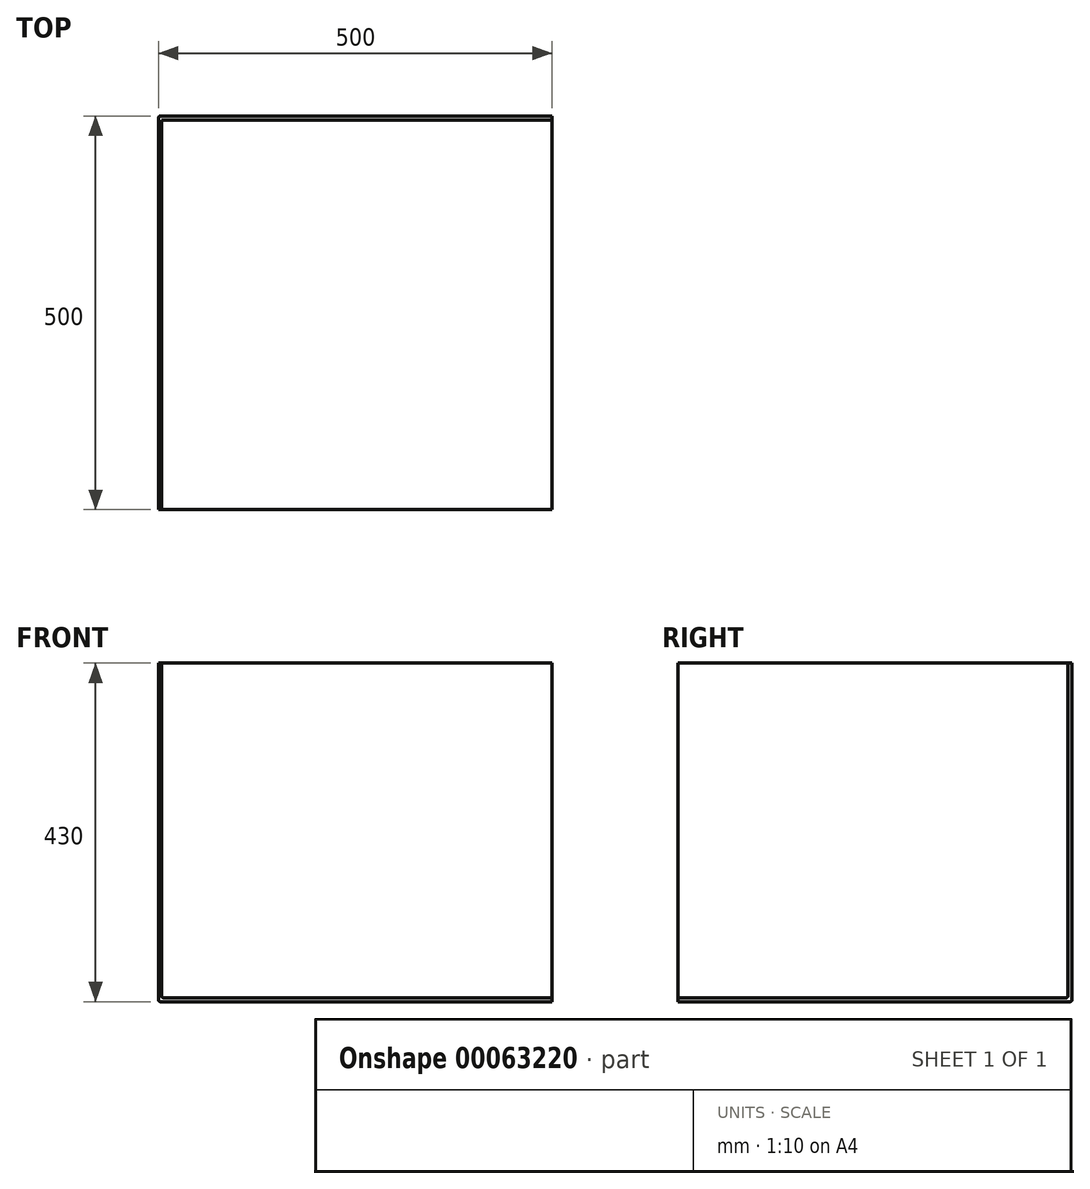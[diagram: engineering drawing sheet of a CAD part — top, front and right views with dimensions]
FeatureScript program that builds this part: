
annotation { "Feature Type Name" : "Feature", "Feature Type Description" : "" }
export const myFeature = defineFeature(function(context is Context, id is Id, definition is map)
    precondition{}
    {
        {
            var Q0;
            Q0=qCreatedBy(makeId("Right.planeOp"),FACE);
            var sketch = newSketch(context, id + "F0", { "sketchPlane" : qUnion([Q0])});
            skLineSegment(sketch, "E0.bottom", {"start": v(0, 0) * mm, "end": v(-5, 0) * mm});
            skLineSegment(sketch, "E0.top", {"start": v(0, 430) * mm, "end": v(-5, 430) * mm});
            skLineSegment(sketch, "E0.left", {"start": v(0, 0) * mm, "end": v(0, 430) * mm});
            skLineSegment(sketch, "E0.right", {"start": v(-5, 0) * mm, "end": v(-5, 430) * mm});
            skSolve(sketch);
        }
        {
            var Q0;
            Q0=makeQuery(id+"F0.imprint","IMPRINT",FACE,{"disambiguationData":[TD([[makeQuery(id+"F0.imprint","IMPRINT",EDGE,{"derivedFrom":sQuery(id+"F0.wireOp",EDGE,"E0.bottom")}),-1.0]])]});
            extrude(context, id + "F1", {"entities" : qUnion([Q0]), "depth" : 500 * mm});
        }
        {
            var Q0;
            Q0=qCreatedBy(makeId("Top.planeOp"),FACE);
            var sketch = newSketch(context, id + "F2", { "sketchPlane" : qUnion([Q0])});
            skLineSegment(sketch, "E1.bottom", {"start": v(0, 0) * mm, "end": v(500, 0) * mm});
            skLineSegment(sketch, "E1.top", {"start": v(0, -500) * mm, "end": v(500, -500) * mm});
            skLineSegment(sketch, "E1.left", {"start": v(0, 0) * mm, "end": v(0, -500) * mm});
            skLineSegment(sketch, "E1.right", {"start": v(500, 0) * mm, "end": v(500, -500) * mm});
            skSolve(sketch);
        }
        {
            var Q0;
            Q0=makeQuery(id+"F2.imprint","IMPRINT",FACE,{"disambiguationData":[TD([[makeQuery(id+"F2.imprint","IMPRINT",EDGE,{"derivedFrom":sQuery(id+"F2.wireOp",EDGE,"E1.bottom")}),-1.0]])]});
            extrude(context, id + "F3", {"entities" : qUnion([Q0]), "operationType" : NewBodyOperationType.ADD, "depth" : 5 * mm});
        }
        {
            var Q0;
            Q0=makeQuery(id+"F1.opExtrude","SWEPT_FACE",FACE,{"disambiguationData":[OSD([sQuery(id+"F0.wireOp",EDGE,"E0.top")])]});
            var sketch = newSketch(context, id + "F4", { "sketchPlane" : qUnion([Q0])});
            skLineSegment(sketch, "E2.bottom", {"start": v(0, 0) * mm, "end": v(4, 0) * mm});
            skLineSegment(sketch, "E2.top", {"start": v(0, -500) * mm, "end": v(4, -500) * mm});
            skLineSegment(sketch, "E2.left", {"start": v(0, 0) * mm, "end": v(0, -500) * mm});
            skLineSegment(sketch, "E2.right", {"start": v(4, 0) * mm, "end": v(4, -500) * mm});
            skSolve(sketch);
        }
        {
            var Q0;
            {var subQ0=sQuery(id+"F4.wireOp",EDGE,"E2.top");Q0=makeQuery(id+"F4.imprint","IMPRINT",FACE,{"disambiguationData":[TD([[makeQuery(id+"F4.imprint","IMPRINT",EDGE,{"derivedFrom":subQ0}),1.0]])]});}
            var Q1;
            {var subQ0=sQuery(id+"F4.wireOp",EDGE,"f364ce6c-c3e6-41b8-b682-b13bb0f9a7eb.top");Q1=makeQuery(id+"F4.imprint","IMPRINT",FACE,{"disambiguationData":[TD([[makeQuery(id+"F4.imprint","IMPRINT",EDGE,{"derivedFrom":subQ0}),-1.0]])]});}
            var Q2;
            Q2=makeQuery(id+"F3.boolean.opBoolean","MERGE",FACE,{"derivedFrom":[makeQuery(id+"F1.opExtrude","SWEPT_FACE",FACE,{"disambiguationData":[OSD([sQuery(id+"F0.wireOp",EDGE,"E0.bottom")])]}),makeQuery(id+"F3.opExtrude","CAP_FACE",FACE,{"disambiguationData":[OSD([sQuery(id+"F2.wireOp",EDGE,"E1.bottom"),sQuery(id+"F2.wireOp",EDGE,"E1.left"),sQuery(id+"F2.wireOp",EDGE,"E1.right"),sQuery(id+"F2.wireOp",EDGE,"b1fd46ea-04c2-4c8c-ba69-9a527e354d7c"),sQuery(id+"F2.wireOp",EDGE,"c21d5cb0-6276-430a-b457-674ba998a2fe")])],"isStart":true})]});
            extrude(context, id + "F5", {"entities" : qUnion([Q0, Q1]), "endBound" : BoundingType.UP_TO_SURFACE, "oppositeDirection" : true, "endBoundEntityFace" : qUnion([Q2]), "depth" : 25 * mm});
        }
        {
            var Q0;
            Q0=makeQuery(id+"F5.opExtrude","SWEPT_BODY",BODY,{"disambiguationData":[OSD([sQuery(id+"F0.wireOp",EDGE,"E0.top"),sQuery(id+"F0.wireOp",EDGE,"E0.right"),sQuery(id+"F4.wireOp",EDGE,"E2.top"),sQuery(id+"F4.wireOp",EDGE,"E2.left"),sQuery(id+"F4.wireOp",EDGE,"E2.right")])]});
            var Q1;
            Q1=makeQuery(id+"F1.opExtrude","SWEPT_BODY",BODY,{"disambiguationData":[OSD([sQuery(id+"F0.wireOp",EDGE,"E0.bottom"),sQuery(id+"F0.wireOp",EDGE,"E0.top"),sQuery(id+"F0.wireOp",EDGE,"E0.left"),sQuery(id+"F0.wireOp",EDGE,"E0.right")])]});
            booleanBodies(context, id + "F6", {"operationType" : BooleanOperationType.UNION, "tools" : qUnion([Q0, Q1])});
        }
        {
            var Q0;
            Q0=makeQuery(id+"F1.opExtrude","CAP_EDGE",EDGE,{"disambiguationData":[OSD([sQuery(id+"F0.wireOp",EDGE,"E0.left")])],"isStart":true});
            var Q1;
            Q1=makeQuery(id+"F1.opExtrude","SWEPT_EDGE",EDGE,{"disambiguationData":[OSD([sQuery(id+"F0.wireOp",EDGE,"E0.bottom"),sQuery(id+"F0.wireOp",EDGE,"E0.left")])]});
            var Q2;
            Q2=makeQuery(id+"F6.opBoolean","MERGE",EDGE,{"derivedFrom":[makeQuery(id+"F3.boolean.opBoolean","MERGE",EDGE,{"derivedFrom":[makeQuery(id+"F1.opExtrude","CAP_EDGE",EDGE,{"disambiguationData":[OSD([sQuery(id+"F0.wireOp",EDGE,"E0.bottom")])],"isStart":true}),makeQuery(id+"F3.opExtrude","CAP_EDGE",EDGE,{"disambiguationData":[OSD([sQuery(id+"F2.wireOp",EDGE,"E1.left")])],"isStart":true})]}),makeQuery(id+"F5.opExtrude","CAP_EDGE",EDGE,{"disambiguationData":[OSD([sQuery(id+"F4.wireOp",EDGE,"E2.left")])],"isStart":false})]});
            var Q3;
            Q3=makeQuery(id+"F3.boolean.opBoolean","INTERSECT",EDGE,{"derivedFrom":[makeQuery(id+"F1.opExtrude","SWEPT_FACE",FACE,{"disambiguationData":[OSD([sQuery(id+"F0.wireOp",EDGE,"E0.right")])]}),makeQuery(id+"F3.opExtrude","CAP_FACE",FACE,{"disambiguationData":[OSD([sQuery(id+"F2.wireOp",EDGE,"E1.bottom"),sQuery(id+"F2.wireOp",EDGE,"E1.top"),sQuery(id+"F2.wireOp",EDGE,"E1.left"),sQuery(id+"F2.wireOp",EDGE,"E1.right")])],"isStart":false})]});
            var Q4;
            Q4=makeQuery(id+"F5.opExtrude","SWEPT_EDGE",EDGE,{"disambiguationData":[OSD([sQuery(id+"F0.wireOp",EDGE,"E0.top"),sQuery(id+"F0.wireOp",EDGE,"E0.right"),sQuery(id+"F4.wireOp",EDGE,"E2.right")])]});
            var Q5;
            Q5=makeQuery(id+"F6.opBoolean","INTERSECT",EDGE,{"derivedFrom":[makeQuery(id+"F3.opExtrude","CAP_FACE",FACE,{"disambiguationData":[OSD([sQuery(id+"F2.wireOp",EDGE,"E1.bottom"),sQuery(id+"F2.wireOp",EDGE,"E1.top"),sQuery(id+"F2.wireOp",EDGE,"E1.left"),sQuery(id+"F2.wireOp",EDGE,"E1.right")])],"isStart":false}),makeQuery(id+"F5.opExtrude","SWEPT_FACE",FACE,{"disambiguationData":[OSD([sQuery(id+"F4.wireOp",EDGE,"E2.right")])]})]});
            fillet(context, id + "F7", {"entities" : qUnion([Q0, Q1, Q2, Q3, Q4, Q5]), "radius" : 2 * mm, "tangentPropagation" : true, "allowEdgeOverflow" : false});
        }
    });
